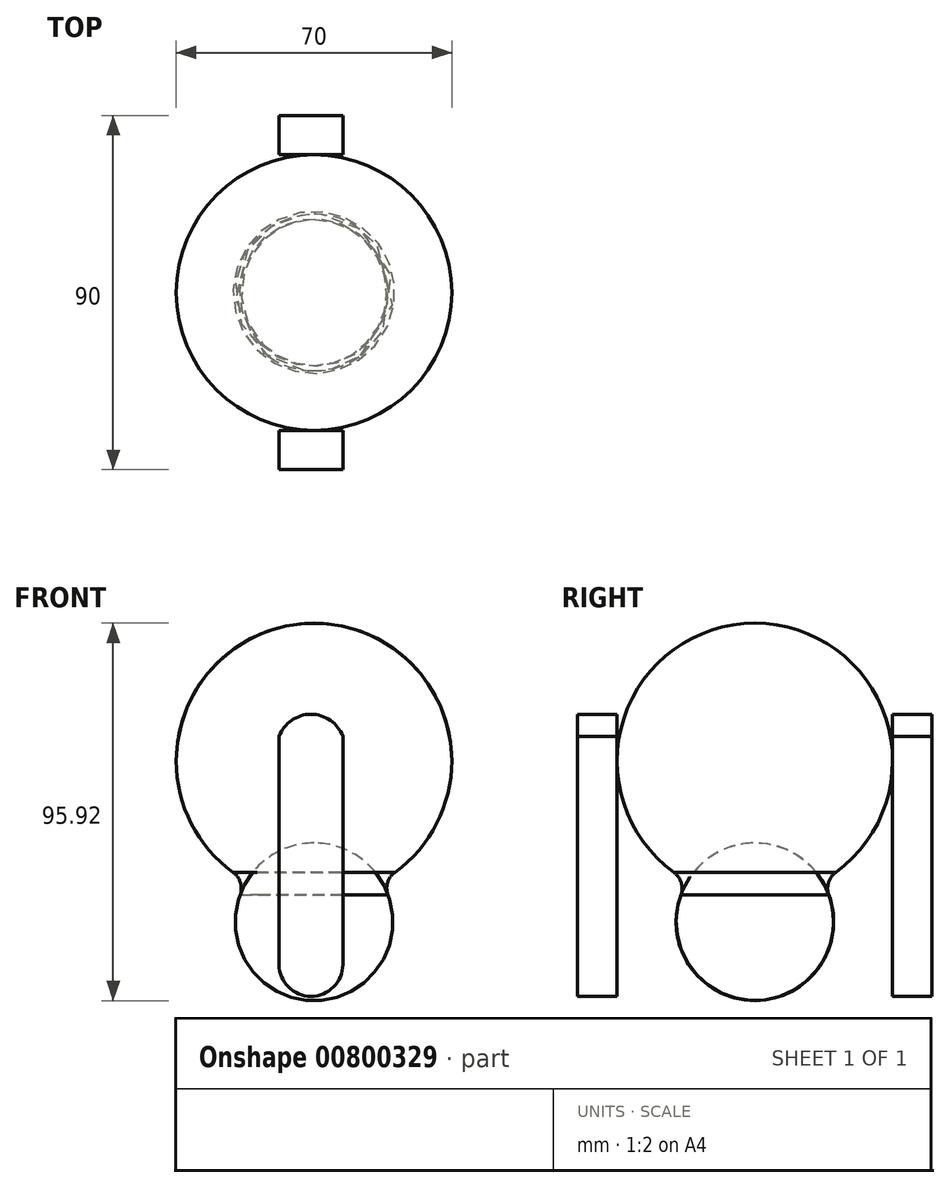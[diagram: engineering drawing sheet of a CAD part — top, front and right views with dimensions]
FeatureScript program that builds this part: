
annotation { "Feature Type Name" : "Feature", "Feature Type Description" : "" }
export const myFeature = defineFeature(function(context is Context, id is Id, definition is map)
    precondition{}
    {
        {
            var Q0;
            Q0=qCreatedBy(makeId("Front.planeOp"),FACE);
            var sketch = newSketch(context, id + "F0", { "sketchPlane" : qUnion([Q0])});
            skArc(sketch, "E0", {"start": v(35, 0) * mm, "mid": v(0, 35) * mm, "end": v(-35, 0) * mm});
            skLineSegment(sketch, "E1", {"start": v(-35, 0) * mm, "end": v(35, 0) * mm});
            skSolve(sketch);
        }
        {
            var Q0;
            Q0 = qSketchRegion(id + "F0", true);
            var Q1;
            Q1=sQuery(id+"F0.wireOp",EDGE,"E1");
            revolve(context, id + "F1", {"surfaceOperationType" : NewSurfaceOperationType.NEW, "entities" : qUnion([Q0]), "axis" : qUnion([Q1]), "revolveType" : RevolveType.FULL});
        }
        {
            var Q0;
            Q0=qCreatedBy(makeId("Front.planeOp"),FACE);
            cPlane(context, id + "F2", {"entities" : qUnion([Q0]), "cplaneType" : CPlaneType.OFFSET, "offset" : 35 * mm, "width" : 150 * mm, "height" : 150 * mm});
        }
        {
            var Q0;
            Q0=qCreatedBy(id+"F2.planeOp",FACE);
            var sketch = newSketch(context, id + "F3", { "sketchPlane" : qUnion([Q0])});
            skLineSegment(sketch, "E2", {"start": v(-8.85, 6.22) * mm, "end": v(-8.85, -51.72) * mm});
            skLineSegment(sketch, "E3", {"start": v(7.33, -51.72) * mm, "end": v(7.33, 6.22) * mm});
            skArc(sketch, "E4", {"start": v(7.33, 6.22) * mm, "mid": v(-0.76, 11.85) * mm, "end": v(-8.85, 6.22) * mm});
            skArc(sketch, "E5", {"start": v(-8.85, -51.72) * mm, "mid": v(-0.76, -59.81) * mm, "end": v(7.33, -51.72) * mm});
            skSolve(sketch);
        }
        {
            var Q0;
            Q0=makeQuery(id+"F3.imprint","IMPRINT",FACE,{"disambiguationData":[TD([[makeQuery(id+"F3.imprint","IMPRINT",EDGE,{"derivedFrom":sQuery(id+"F3.wireOp",EDGE,"E2")}),1.0]])]});
            extrude(context, id + "F4", {"entities" : qUnion([Q0]), "depth" : 10 * mm, "offsetDistance" : 25 * mm});
        }
        {
            var Q0;
            Q0=makeQuery(id+"F4.opExtrude","SWEPT_BODY",BODY,{"disambiguationData":[OSD([sQuery(id+"F3.wireOp",EDGE,"E2"),sQuery(id+"F3.wireOp",EDGE,"E3"),sQuery(id+"F3.wireOp",EDGE,"E4"),sQuery(id+"F3.wireOp",EDGE,"E5")])]});
            var Q1;
            Q1=qCreatedBy(makeId("Front.planeOp"),FACE);
            mirror(context, id + "F5", {"entities" : qUnion([Q0]), "mirrorPlane" : qUnion([Q1])});
        }
        {
            var Q0;
            Q0=qCreatedBy(makeId("Right.planeOp"),FACE);
            var sketch = newSketch(context, id + "F6", { "sketchPlane" : qUnion([Q0])});
            skArc(sketch, "E6", {"start": v(-20, -41) * mm, "mid": v(0.12, -60.86) * mm, "end": v(20, -40.77) * mm});
            skLineSegment(sketch, "E7", {"start": v(-20, -41) * mm, "end": v(20, -40.77) * mm});
            skSolve(sketch);
        }
        {
            var Q0;
            Q0 = qSketchRegion(id + "F6", true);
            var Q1;
            Q1=sQuery(id+"F6.wireOp",EDGE,"E7");
            revolve(context, id + "F7", {"operationType" : NewBodyOperationType.ADD, "surfaceOperationType" : NewSurfaceOperationType.NEW, "entities" : qUnion([Q0]), "axis" : qUnion([Q1]), "revolveType" : RevolveType.FULL});
        }
        {
            var Q0;
            Q0=makeQuery(id+"F7.boolean.opBoolean","INTERSECT",EDGE,{"derivedFrom":[makeQuery(id+"F1.opRevolve","SWEPT_FACE",FACE,{"disambiguationData":[OSD([sQuery(id+"F0.wireOp",EDGE,"E0")])]}),makeQuery(id+"F7.opRevolve","SWEPT_FACE",FACE,{"disambiguationData":[OSD([sQuery(id+"F6.wireOp",EDGE,"E6")])]})]});
            fillet(context, id + "F8", {"entities" : qUnion([Q0]), "radius" : 5 * mm, "tangentPropagation" : true, "allowEdgeOverflow" : false});
        }
    });
